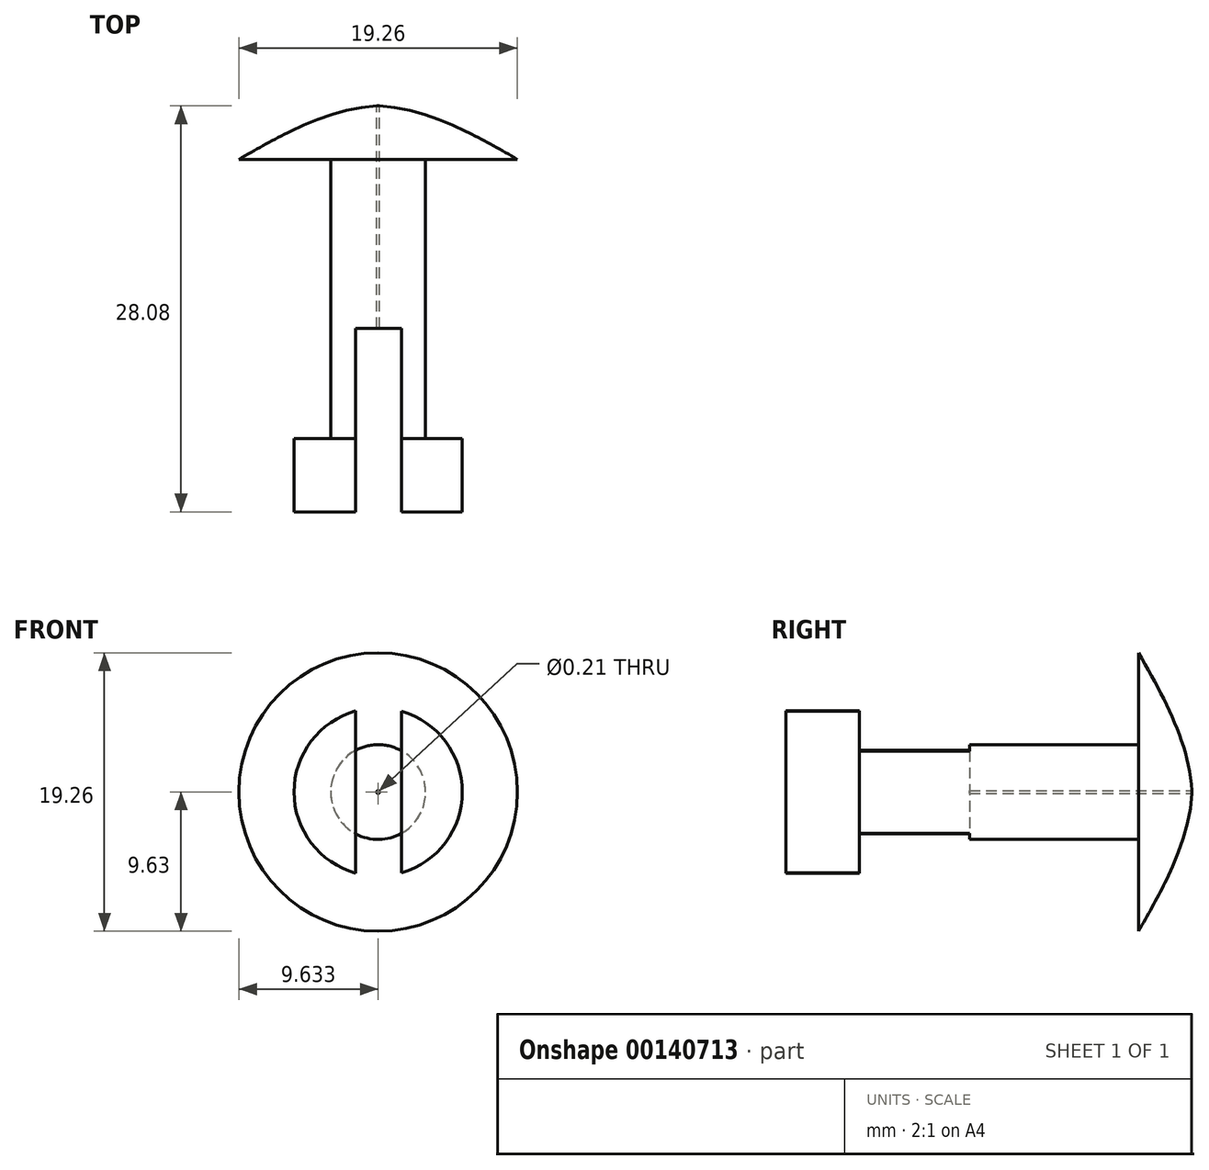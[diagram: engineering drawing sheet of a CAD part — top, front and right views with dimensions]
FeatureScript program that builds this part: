
annotation { "Feature Type Name" : "Feature", "Feature Type Description" : "" }
export const myFeature = defineFeature(function(context is Context, id is Id, definition is map)
    precondition{}
    {
        {
            var Q0;
            Q0=qCreatedBy(makeId("Top.planeOp"),FACE);
            var sketch = newSketch(context, id + "F0", { "sketchPlane" : qUnion([Q0])});
            skLineSegment(sketch, "E0", {"start": v(-29.08, 31.2) * mm, "end": v(-29.08, 11.9) * mm});
            skLineSegment(sketch, "E1", {"start": v(-29.08, 31.2) * mm, "end": v(-35.43, 31.2) * mm});
            skLineSegment(sketch, "E2", {"start": v(-29.08, 11.9) * mm, "end": v(-31.62, 11.9) * mm});
            skFitSpline(sketch, "E3", {"points": [v(-35.43, 31.2) * mm, v(-23.87, 34.86) * mm, v(-2.83, 22.57) * mm], "startDerivative": vector(26.3, 15) * mm, "endDerivative": vector(38.22, -29.69) * mm});
            skLineSegment(sketch, "E4", {"start": v(-25.9, 20.63) * mm, "end": v(-25.9, 34.9) * mm});
            skPoint(sketch, "E5.2.internal.orphan", {"position": v(-7.94, 0) * mm});
            skPoint(sketch, "E6.end.orphan", {"position": v(-31.62, 0) * mm});
            skLineSegment(sketch, "E7", {"start": v(-31.62, 11.9) * mm, "end": v(-31.62, 6.82) * mm});
            skLineSegment(sketch, "E8", {"start": v(-25.9, 20.63) * mm, "end": v(-25.9, 6.82) * mm});
            skLineSegment(sketch, "E9", {"start": v(-31.62, 6.82) * mm, "end": v(-25.9, 6.82) * mm});
            skPoint(sketch, "E10.2.internal.orphan", {"position": v(-6.71, 6.82) * mm});
            skSolve(sketch);
        }
        {
            var Q0;
            Q0=qCreatedBy(makeId("Top.planeOp"),FACE);
            var sketch = newSketch(context, id + "F1", { "sketchPlane" : qUnion([Q0])});
            skLineSegment(sketch, "E11", {"start": v(-25.8, 34.9) * mm, "end": v(-25.8, 0) * mm});
            skSolve(sketch);
        }
        {
            var Q0;
            Q0=makeQuery(id+"F0.imprint","IMPRINT",FACE,{"disambiguationData":[TD([[makeQuery(id+"F0.imprint","IMPRINT",EDGE,{"derivedFrom":sQuery(id+"F0.wireOp",EDGE,"E0")}),1.0]])]});
            var Q1;
            Q1=sQuery(id+"F1.wireOp",EDGE,"E11");
            revolve(context, id + "F2", {"entities" : qUnion([Q0]), "axis" : qUnion([Q1]), "revolveType" : RevolveType.FULL});
        }
        {
            var Q0;
            Q0=makeQuery(id+"F2.opRevolve","SWEPT_FACE",FACE,{"disambiguationData":[OSD([sQuery(id+"F0.wireOp",EDGE,"E9")])]});
            var sketch = newSketch(context, id + "F3", { "sketchPlane" : qUnion([Q0])});
            skLineSegment(sketch, "E12", {"start": v(-25.8, 0) * mm, "end": v(-25.8, 5.82) * mm});
            skLineSegment(sketch, "E13", {"start": v(-25.8, 2.9) * mm, "end": v(-25.16, 2.9) * mm});
            skLineSegment(sketch, "E14", {"start": v(-25.8, 2.9) * mm, "end": v(-27.04, 2.9) * mm});
            skSolve(sketch);
        }
        {
            var Q0;
            {var subQ0=sQuery(id+"F0.wireOp",EDGE,"E9");Q0=makeQuery(id+"F3.imprint","IMPRINT",FACE,{"disambiguationData":[TD([[makeQuery(id+"F3.imprint","IMPRINT",EDGE,{"derivedFrom":makeQuery(id+"F2.opRevolve","SWEPT_EDGE",EDGE,{"disambiguationData":[OSD([sQuery(id+"F0.wireOp",EDGE,"E7"),subQ0])]})}),-1.0]])]});}
            var sketch = newSketch(context, id + "F4", { "sketchPlane" : qUnion([Q0])});
            skLineSegment(sketch, "E15.bottom", {"start": v(-24.17, 6.35) * mm, "end": v(-27.34, 6.35) * mm});
            skLineSegment(sketch, "E15.top", {"start": v(-24.17, -6.35) * mm, "end": v(-27.34, -6.35) * mm});
            skLineSegment(sketch, "E15.left", {"start": v(-24.17, 6.35) * mm, "end": v(-24.17, -6.35) * mm});
            skLineSegment(sketch, "E15.right", {"start": v(-27.34, 6.35) * mm, "end": v(-27.34, -6.35) * mm});
            skPoint(sketch, "E15.middle", {"position": v(-25.76, 0) * mm});
            skSolve(sketch);
        }
        {
            var Q0;
            Q0 = qSketchRegion(id + "F4", true);
            extrude(context, id + "F5", {"entities" : qUnion([Q0]), "operationType" : NewBodyOperationType.REMOVE, "oppositeDirection" : true, "depth" : 12.7 * mm});
        }
    });
